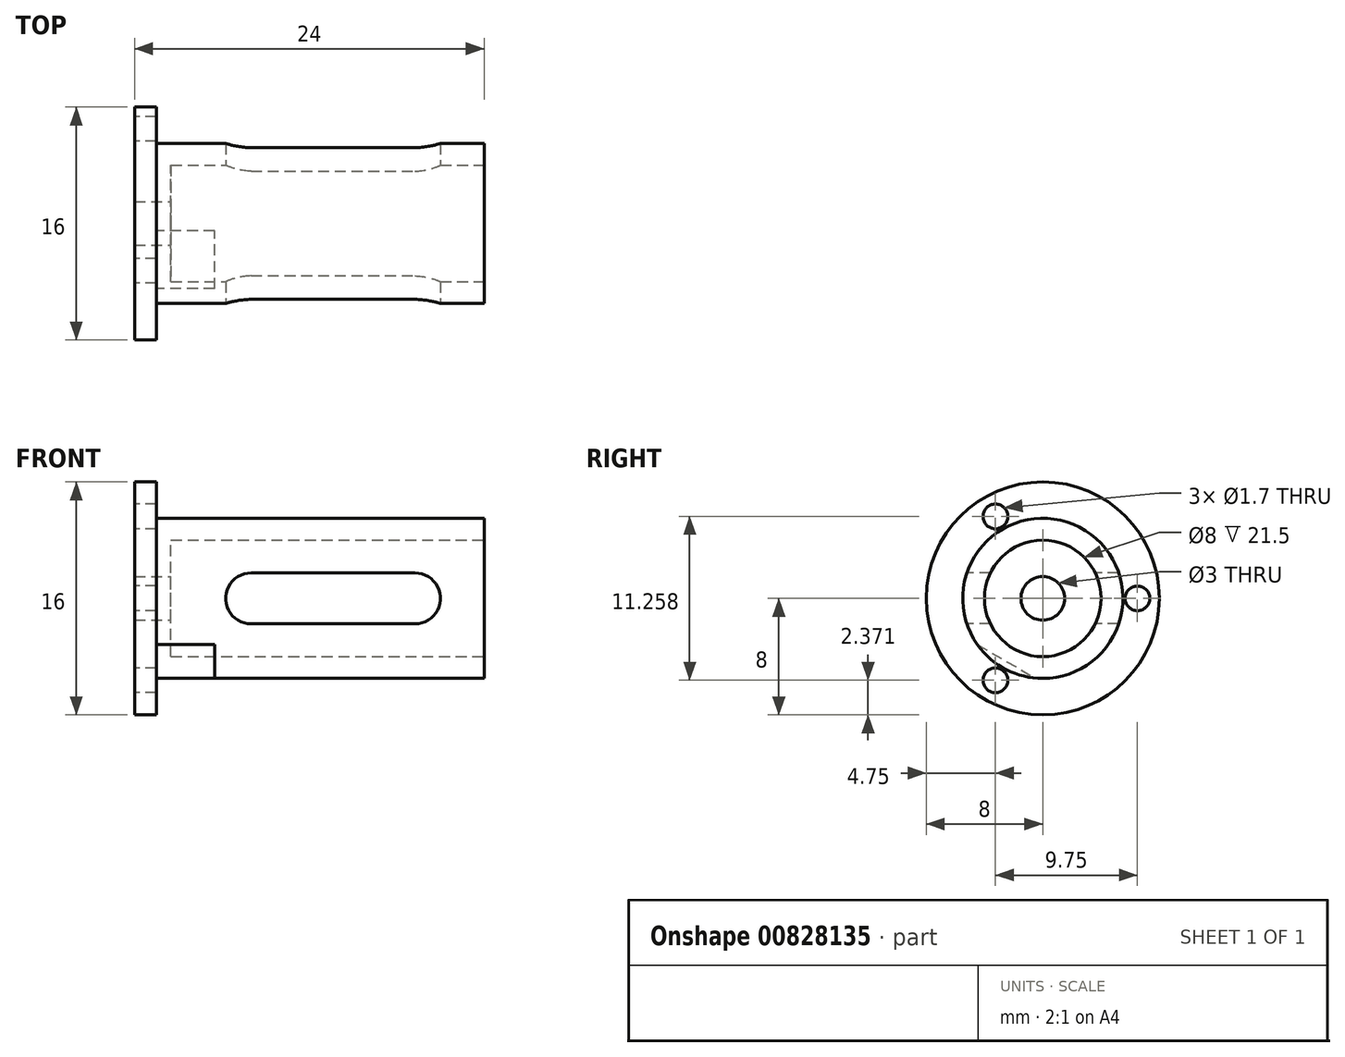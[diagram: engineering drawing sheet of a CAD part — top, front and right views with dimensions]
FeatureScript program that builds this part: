
annotation { "Feature Type Name" : "Feature", "Feature Type Description" : "" }
export const myFeature = defineFeature(function(context is Context, id is Id, definition is map)
    precondition{}
    {
        {
            var Q0;
            Q0=qCreatedBy(makeId("Right.planeOp"),FACE);
            var sketch = newSketch(context, id + "F0", { "sketchPlane" : qUnion([Q0])});
            skCircle(sketch, "E0", {"center": v(0, 0) * mm, "radius": 8 * mm});
            skSolve(sketch);
        }
        {
            var Q0;
            Q0 = qSketchRegion(id + "F0", true);
            extrude(context, id + "F1", {"entities" : qUnion([Q0]), "depth" : 1.5 * mm, "offsetDistance" : 25 * mm});
        }
        {
            var Q0;
            Q0=makeQuery(id+"F1.opExtrude","CAP_FACE",FACE,{"disambiguationData":[OSD([sQuery(id+"F0.wireOp",EDGE,"E0")])],"isStart":false});
            var sketch = newSketch(context, id + "F2", { "sketchPlane" : qUnion([Q0])});
            skCircle(sketch, "E1", {"center": v(0, 0) * mm, "radius": 5.5 * mm});
            skSolve(sketch);
        }
        {
            var Q0;
            Q0 = qSketchRegion(id + "F2", true);
            extrude(context, id + "F3", {"entities" : qUnion([Q0]), "operationType" : NewBodyOperationType.ADD, "depth" : 22.5 * mm, "offsetDistance" : 25 * mm});
        }
        {
            var Q0;
            Q0=makeQuery(id+"F3.opExtrude","CAP_FACE",FACE,{"disambiguationData":[OSD([sQuery(id+"F2.wireOp",EDGE,"E1")])],"isStart":false});
            var sketch = newSketch(context, id + "F4", { "sketchPlane" : qUnion([Q0])});
            skCircle(sketch, "E2", {"center": v(0, 0) * mm, "radius": 4 * mm});
            skSolve(sketch);
        }
        {
            var Q0;
            Q0 = qSketchRegion(id + "F4", true);
            extrude(context, id + "F5", {"entities" : qUnion([Q0]), "operationType" : NewBodyOperationType.REMOVE, "oppositeDirection" : true, "depth" : 21.5 * mm, "offsetDistance" : 25 * mm});
        }
        {
            var Q0;
            Q0=qCreatedBy(makeId("Right.planeOp"),FACE);
            var sketch = newSketch(context, id + "F6", { "sketchPlane" : qUnion([Q0])});
            skPoint(sketch, "E3", {"position": v(-3.25, 5.63) * mm});
            skPoint(sketch, "E4", {"position": v(6.5, 0) * mm});
            skPoint(sketch, "E5", {"position": v(-3.25, -5.63) * mm});
            skCircle(sketch, "E6", {"center": v(0, 0) * mm, "radius": 6.5 * mm, "construction": true});
            skLineSegment(sketch, "E7", {"start": v(0, 0) * mm, "end": v(-3.25, -5.63) * mm, "construction": true});
            skLineSegment(sketch, "E8", {"start": v(0, 0) * mm, "end": v(-3.25, 5.63) * mm, "construction": true});
            skSolve(sketch);
        }
        {
            var Q0;
            Q0=sQuery(id+"F6.wireOp",VERTEX,"E3");
            var Q1;
            Q1=sQuery(id+"F6.wireOp",VERTEX,"E4");
            var Q2;
            Q2=sQuery(id+"F6.wireOp",VERTEX,"E5");
            var Q3;
            Q3=makeQuery(id+"F1.opExtrude","SWEPT_BODY",BODY,{"disambiguationData":[OSD([sQuery(id+"F0.wireOp",EDGE,"E0")])]});
            hole(context, id + "F7", {"style" : HoleStyle.SIMPLE, "endStyle" : HoleEndStyle.THROUGH, "oppositeDirection" : true, "standardTappedOrClearance" : lookupTablePath({ "standard" : "ISO", "size" : "1.7", "type" : "Drilled" }), "standardBlindInLast" : lookupTablePath({ "standard" : "ISO", "size" : "1.7", "type" : "Drilled" }), "holeDiameter" : 1.7 * mm, "majorDiameter" : 5 * mm, "isTappedThrough" : true, "tappedDepth" : 7.3 * mm, "tapClearance" : 3, "locations" : qUnion([Q0, Q1, Q2]), "scope" : qUnion([Q3])});
        }
        {
            var Q0;
            Q0=makeQuery(id+"F5.boolean.opBoolean","COPY",FACE,{"derivedFrom":makeQuery(id+"F5.opExtrude","CAP_FACE",FACE,{"disambiguationData":[OSD([sQuery(id+"F4.wireOp",EDGE,"E2")])],"isStart":false})});
            var sketch = newSketch(context, id + "F8", { "sketchPlane" : qUnion([Q0])});
            skPoint(sketch, "E9", {"position": v(0, 0) * mm});
            skSolve(sketch);
        }
        {
            var Q0;
            Q0=sQuery(id+"F8.wireOp",VERTEX,"E9");
            var Q1;
            Q1=makeQuery(id+"F1.opExtrude","SWEPT_BODY",BODY,{"disambiguationData":[OSD([sQuery(id+"F0.wireOp",EDGE,"E0")])]});
            hole(context, id + "F9", {"style" : HoleStyle.SIMPLE, "endStyle" : HoleEndStyle.THROUGH, "standardTappedOrClearance" : lookupTablePath({ "standard" : "ISO", "size" : "3", "type" : "Drilled" }), "standardBlindInLast" : lookupTablePath({ "standard" : "ISO", "size" : "3", "type" : "Drilled" }), "holeDiameter" : 3 * mm, "majorDiameter" : 5 * mm, "isTappedThrough" : true, "tappedDepth" : 7.3 * mm, "tapClearance" : 3, "locations" : qUnion([Q0]), "scope" : qUnion([Q1])});
        }
        {
            var Q0;
            Q0=qCreatedBy(makeId("Front.planeOp"),FACE);
            var sketch = newSketch(context, id + "F10", { "sketchPlane" : qUnion([Q0])});
            skArc(sketch, "E10", {"start": v(19.25, -1.75) * mm, "mid": v(21, 0) * mm, "end": v(19.25, 1.75) * mm});
            skArc(sketch, "E11", {"start": v(8, 1.75) * mm, "mid": v(6.25, 0) * mm, "end": v(8, -1.75) * mm});
            skLineSegment(sketch, "E12", {"start": v(8, 1.75) * mm, "end": v(19.25, 1.75) * mm});
            skLineSegment(sketch, "E13", {"start": v(8, -1.75) * mm, "end": v(19.25, -1.75) * mm});
            skSolve(sketch);
        }
        {
            var Q0;
            Q0 = qSketchRegion(id + "F10", true);
            extrude(context, id + "F11", {"entities" : qUnion([Q0]), "operationType" : NewBodyOperationType.REMOVE, "endBound" : BoundingType.THROUGH_ALL, "oppositeDirection" : true, "depth" : 25 * mm, "offsetDistance" : 25 * mm, "hasSecondDirection" : true, "secondDirectionOppositeDirection" : false, "secondDirectionDepth" : 25 * mm});
        }
        {
            var Q0;
            Q0=makeQuery(id+"F1.opExtrude","CAP_FACE",FACE,{"disambiguationData":[OSD([sQuery(id+"F0.wireOp",EDGE,"E0")])],"isStart":false});
            var sketch = newSketch(context, id + "F12", { "sketchPlane" : qUnion([Q0])});
            skLineSegment(sketch, "E14", {"start": v(-4.67, -3.08) * mm, "end": v(-0.33, -5.58) * mm});
            skLineSegment(sketch, "E15", {"start": v(-0.33, -5.58) * mm, "end": v(-0.58, -6.01) * mm});
            skLineSegment(sketch, "E16", {"start": v(-0.58, -6.01) * mm, "end": v(-4.92, -3.51) * mm});
            skLineSegment(sketch, "E17", {"start": v(-4.67, -3.08) * mm, "end": v(-4.92, -3.51) * mm});
            skLineSegment(sketch, "E18", {"start": v(-3.25, -5.63) * mm, "end": v(0, 0) * mm, "construction": true});
            skSolve(sketch);
        }
        {
            var Q0;
            {var subQ0=sQuery(id+"F12.wireOp",EDGE,"E14");var subQ1=makeQuery(id+"F3.opExtrude","CAP_EDGE",EDGE,{"disambiguationData":[OSD([sQuery(id+"F2.wireOp",EDGE,"E1")])],"isStart":true});var subQ2=makeQuery(id+"F12.imprint","INTERSECT",VERTEX,{"disambiguationData":[OD(0.0)],"derivedFrom":[subQ1,subQ0]});Q0=makeQuery(id+"F12.imprint","IMPRINT",FACE,{"disambiguationData":[TD([[makeQuery(id+"F12.imprint","IMPRINT",EDGE,{"disambiguationData":[TD([[subQ2,-1.0]])],"derivedFrom":subQ0}),-1.0]])]});}
            var Q1;
            Q1=sQuery(id+"F12.wireOp",EDGE,"E16");
            var Q2;
            Q2=sQuery(id+"F12.wireOp",EDGE,"E15");
            var Q3;
            Q3=sQuery(id+"F12.wireOp",EDGE,"E14");
            var Q4;
            Q4=sQuery(id+"F12.wireOp",EDGE,"E17");
            extrude(context, id + "F13", {"entities" : qUnion([Q0]), "operationType" : NewBodyOperationType.REMOVE, "surfaceEntities" : qUnion([Q1, Q2, Q3, Q4]), "depth" : 4 * mm, "offsetDistance" : 25 * mm});
        }
    });
